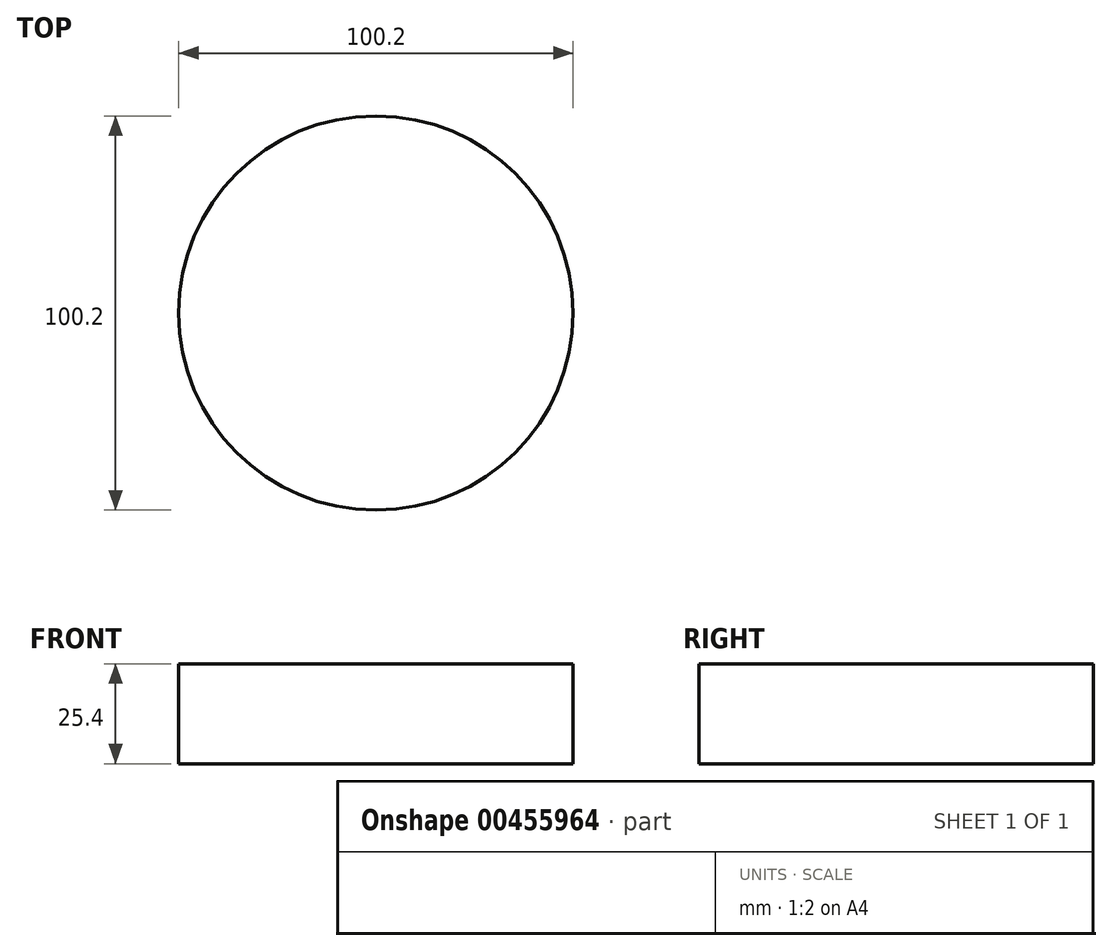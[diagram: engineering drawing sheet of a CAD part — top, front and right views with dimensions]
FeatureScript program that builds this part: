
annotation { "Feature Type Name" : "Feature", "Feature Type Description" : "" }
export const myFeature = defineFeature(function(context is Context, id is Id, definition is map)
    precondition{}
    {
        {
            var Q0;
            Q0=qCreatedBy(makeId("Top.planeOp"),FACE);
            var sketch = newSketch(context, id + "F0", { "sketchPlane" : qUnion([Q0])});
            skCircle(sketch, "E0", {"center": v(0, 0) * mm, "radius": 50.1 * mm});
            skSolve(sketch);
        }
        {
            var Q0;
            Q0 = qSketchRegion(id + "F0", true);
            extrude(context, id + "F1", {"entities" : qUnion([Q0]), "depth" : 25.4 * mm});
        }
    });
